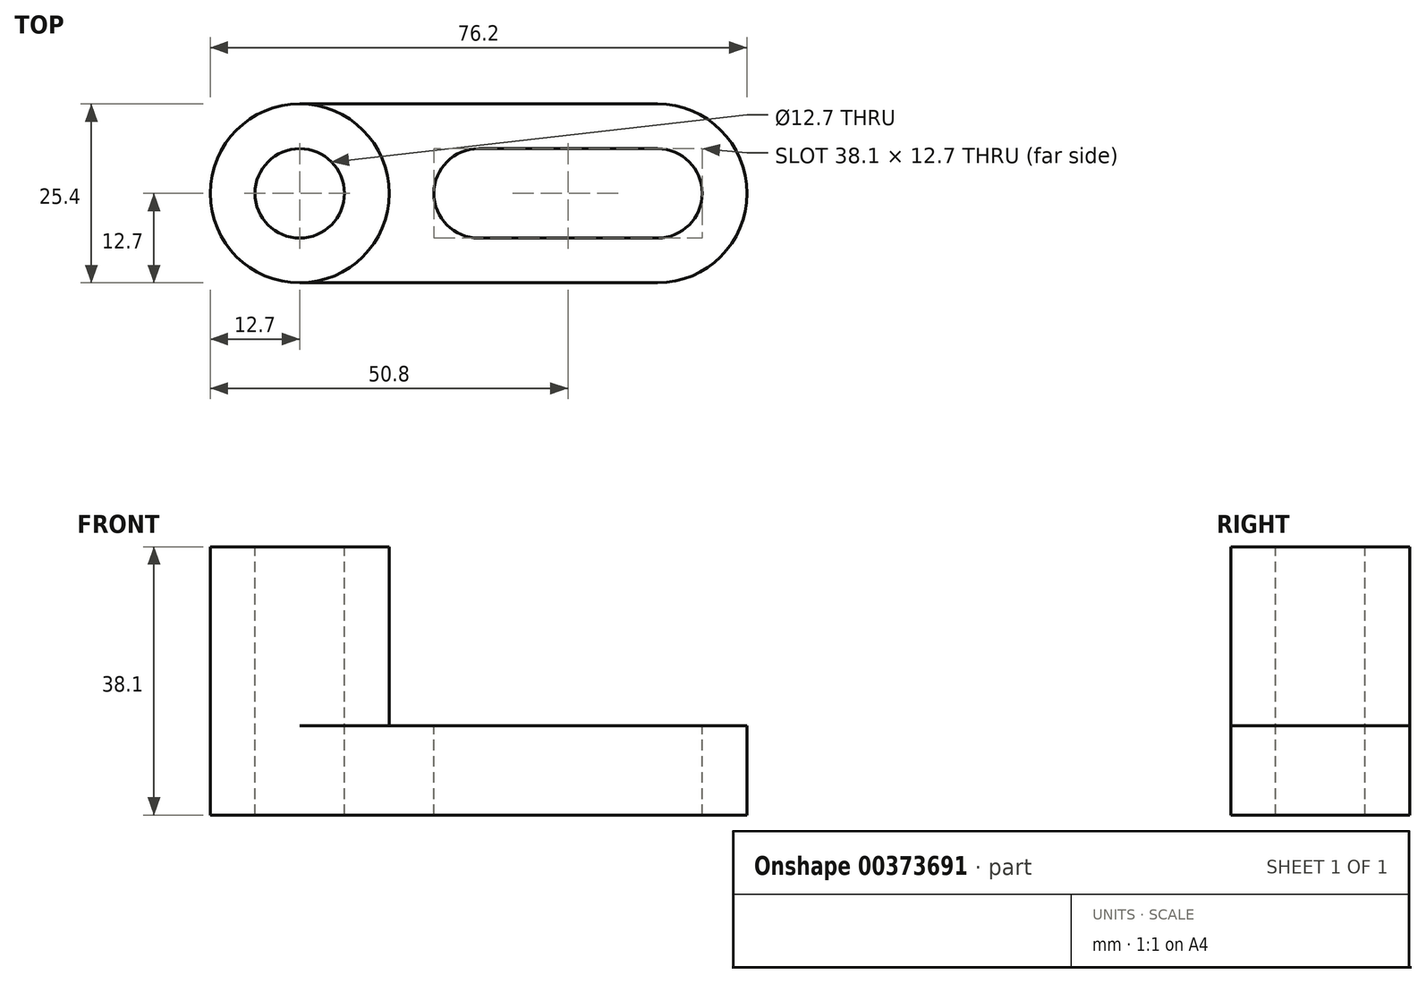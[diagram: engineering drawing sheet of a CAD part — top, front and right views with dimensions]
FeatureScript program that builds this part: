
annotation { "Feature Type Name" : "Feature", "Feature Type Description" : "" }
export const myFeature = defineFeature(function(context is Context, id is Id, definition is map)
    precondition{}
    {
        {
            var Q0;
            Q0=qCreatedBy(makeId("Front.planeOp"),FACE);
            var sketch = newSketch(context, id + "F0", { "sketchPlane" : qUnion([Q0])});
            skLineSegment(sketch, "E0", {"start": v(0, 0) * mm, "end": v(76.2, 0) * mm});
            skLineSegment(sketch, "E1", {"start": v(76.2, 12.7) * mm, "end": v(25.4, 12.7) * mm});
            skLineSegment(sketch, "E2", {"start": v(25.4, 12.7) * mm, "end": v(25.4, 38.1) * mm});
            skLineSegment(sketch, "E3", {"start": v(25.4, 38.1) * mm, "end": v(0, 38.1) * mm});
            skLineSegment(sketch, "E4", {"start": v(0, 38.1) * mm, "end": v(0, 0) * mm});
            skLineSegment(sketch, "E5", {"start": v(76.2, 12.7) * mm, "end": v(76.2, 0) * mm});
            skSolve(sketch);
        }
        {
            var Q0;
            Q0=makeQuery(id+"F0.imprint","IMPRINT",FACE,{"disambiguationData":[TD([[makeQuery(id+"F0.imprint","IMPRINT",EDGE,{"derivedFrom":sQuery(id+"F0.wireOp",EDGE,"E0")}),1.0]])]});
            extrude(context, id + "F1", {"entities" : qUnion([Q0]), "depth" : 25.4 * mm});
        }
        {
            var Q0;
            Q0=makeQuery(id+"F1.opExtrude","SWEPT_FACE",FACE,{"disambiguationData":[OSD([sQuery(id+"F0.wireOp",EDGE,"E3")])]});
            var sketch = newSketch(context, id + "F2", { "sketchPlane" : qUnion([Q0])});
            skCircle(sketch, "E6", {"center": v(12.7, -12.7) * mm, "radius": 12.7 * mm});
            skPoint(sketch, "E6.centerSnap0", {"position": v(25.4, -12.7) * mm});
            skPoint(sketch, "E6.centerSnap1", {"position": v(12.7, 0) * mm});
            skCircle(sketch, "E7", {"center": v(12.7, -12.7) * mm, "radius": 6.35 * mm});
            skSolve(sketch);
        }
        {
            var Q0;
            {var subQ0=sQuery(id+"F2.wireOp",EDGE,"E6");var subQ1=sQuery(id+"F0.wireOp",EDGE,"E3");var subQ2=makeQuery(id+"F1.opExtrude","CAP_EDGE",EDGE,{"disambiguationData":[OSD([subQ1])],"isStart":true});var subQ3=makeQuery(id+"F2.imprint","INTERSECT",VERTEX,{"derivedFrom":[subQ2,subQ0]});Q0=makeQuery(id+"F2.imprint","IMPRINT",FACE,{"disambiguationData":[TD([[makeQuery(id+"F2.imprint","IMPRINT",EDGE,{"disambiguationData":[TD([[subQ3,-1.0]])],"derivedFrom":subQ0}),-1.0]])]});}
            var Q1;
            {var subQ0=sQuery(id+"F2.wireOp",EDGE,"E6");var subQ1=sQuery(id+"F0.wireOp",EDGE,"E3");var subQ4=makeQuery(id+"F1.opExtrude","CAP_EDGE",EDGE,{"disambiguationData":[OSD([subQ1])],"isStart":false});var subQ5=makeQuery(id+"F2.imprint","INTERSECT",VERTEX,{"derivedFrom":[subQ4,subQ0]});Q1=makeQuery(id+"F2.imprint","IMPRINT",FACE,{"disambiguationData":[TD([[makeQuery(id+"F2.imprint","IMPRINT",EDGE,{"disambiguationData":[TD([[subQ5,1.0]])],"derivedFrom":subQ0}),-1.0]])]});}
            var Q2;
            Q2=makeQuery(id+"F2.imprint","IMPRINT",FACE,{"disambiguationData":[TD([[makeQuery(id+"F2.imprint","IMPRINT",EDGE,{"derivedFrom":sQuery(id+"F2.wireOp",EDGE,"E7")}),1.0]])]});
            extrude(context, id + "F3", {"entities" : qUnion([Q0, Q1, Q2]), "operationType" : NewBodyOperationType.REMOVE, "oppositeDirection" : true, "depth" : 50.8 * mm});
        }
        {
            var Q0;
            {var subQ0=sQuery(id+"F2.wireOp",EDGE,"E6");var subQ1=sQuery(id+"F0.wireOp",EDGE,"E3");var subQ2=makeQuery(id+"F1.opExtrude","CAP_EDGE",EDGE,{"disambiguationData":[OSD([subQ1])],"isStart":true});var subQ3=makeQuery(id+"F2.imprint","INTERSECT",VERTEX,{"derivedFrom":[subQ2,subQ0]});Q0=makeQuery(id+"F2.imprint","IMPRINT",FACE,{"disambiguationData":[TD([[makeQuery(id+"F2.imprint","IMPRINT",EDGE,{"disambiguationData":[TD([[subQ3,1.0]])],"derivedFrom":subQ0}),-1.0]])]});}
            var Q1;
            {var subQ0=sQuery(id+"F2.wireOp",EDGE,"E6");var subQ1=sQuery(id+"F0.wireOp",EDGE,"E3");var subQ4=makeQuery(id+"F1.opExtrude","CAP_EDGE",EDGE,{"disambiguationData":[OSD([subQ1])],"isStart":false});var subQ5=makeQuery(id+"F2.imprint","INTERSECT",VERTEX,{"derivedFrom":[subQ4,subQ0]});Q1=makeQuery(id+"F2.imprint","IMPRINT",FACE,{"disambiguationData":[TD([[makeQuery(id+"F2.imprint","IMPRINT",EDGE,{"disambiguationData":[TD([[subQ5,-1.0]])],"derivedFrom":subQ0}),-1.0]])]});}
            extrude(context, id + "F4", {"entities" : qUnion([Q0, Q1]), "operationType" : NewBodyOperationType.REMOVE, "oppositeDirection" : true, "depth" : 25.4 * mm});
        }
        {
            var Q0;
            {var subQ0=sQuery(id+"F0.wireOp",EDGE,"E3");var subQ1=makeQuery(id+"F1.opExtrude","CAP_EDGE",EDGE,{"disambiguationData":[OSD([subQ0])],"isStart":false});var subQ2=sQuery(id+"F0.wireOp",EDGE,"E2");var subQ3=makeQuery(id+"F1.opExtrude","SWEPT_EDGE",EDGE,{"disambiguationData":[OSD([subQ2,subQ0])]});var subQ4=makeQuery(id+"F2.imprint","INTERSECT",VERTEX,{"derivedFrom":[subQ3,subQ1]});var subQ5=sQuery(id+"F2.wireOp",EDGE,"E6");var subQ6=makeQuery(id+"F2.imprint","INTERSECT",VERTEX,{"derivedFrom":[subQ1,subQ5]});var subQ8=makeQuery(id+"F1.opExtrude","CAP_EDGE",EDGE,{"disambiguationData":[OSD([subQ0])],"isStart":true});var subQ9=makeQuery(id+"F2.imprint","INTERSECT",VERTEX,{"derivedFrom":[subQ3,subQ8]});var subQ10=makeQuery(id+"F2.imprint","INTERSECT",VERTEX,{"derivedFrom":[subQ8,subQ5]});Q0=makeQuery(id+"F4.boolean.opBoolean","MERGE",FACE,{"derivedFrom":[makeQuery(id+"F1.opExtrude","SWEPT_FACE",FACE,{"disambiguationData":[OSD([sQuery(id+"F0.wireOp",EDGE,"E1")])]}),makeQuery(id+"F4.opExtrude","CAP_FACE",FACE,{"disambiguationData":[OSD([subQ2,subQ0,subQ5]),TDD([makeQuery(id+"F2.imprint","IMPRINT",EDGE,{"disambiguationData":[TD([[subQ10,1.0]])],"derivedFrom":subQ5}),makeQuery(id+"F2.imprint","IMPRINT",EDGE,{"disambiguationData":[TD([[subQ9,1.0]])],"derivedFrom":subQ3}),makeQuery(id+"F2.imprint","IMPRINT",EDGE,{"disambiguationData":[TD([[subQ10,1.0]])],"derivedFrom":subQ8})])],"isStart":false}),makeQuery(id+"F4.opExtrude","CAP_FACE",FACE,{"disambiguationData":[OSD([subQ2,subQ0,subQ5]),TDD([makeQuery(id+"F2.imprint","IMPRINT",EDGE,{"disambiguationData":[TD([[subQ6,-1.0]])],"derivedFrom":subQ5}),makeQuery(id+"F2.imprint","IMPRINT",EDGE,{"disambiguationData":[TD([[subQ4,-1.0]])],"derivedFrom":subQ3}),makeQuery(id+"F2.imprint","IMPRINT",EDGE,{"disambiguationData":[TD([[subQ6,1.0]])],"derivedFrom":subQ1})])],"isStart":false})]});}
            var sketch = newSketch(context, id + "F5", { "sketchPlane" : qUnion([Q0])});
            skCircle(sketch, "E8", {"center": v(38.1, -12.7) * mm, "radius": 6.35 * mm});
            skPoint(sketch, "E8.centerSnap0", {"position": v(25.4, -12.7) * mm});
            skCircle(sketch, "E9", {"center": v(63.5, -12.7) * mm, "radius": 6.35 * mm});
            skLineSegment(sketch, "E10", {"start": v(63.5, -19.05) * mm, "end": v(38.1, -19.05) * mm});
            skLineSegment(sketch, "E11", {"start": v(38.1, -19.05) * mm, "end": v(38.1, -6.35) * mm});
            skLineSegment(sketch, "E12", {"start": v(38.1, -6.35) * mm, "end": v(63.5, -6.35) * mm});
            skLineSegment(sketch, "E13", {"start": v(63.5, -6.35) * mm, "end": v(63.5, -19.05) * mm});
            skArc(sketch, "E14", {"start": v(63.5, -25.4) * mm, "mid": v(76.2, -12.7) * mm, "end": v(63.5, 0) * mm});
            skSolve(sketch);
        }
        {
            var Q0;
            {var subQ0=sQuery(id+"F5.wireOp",EDGE,"E13");Q0=makeQuery(id+"F5.imprint","IMPRINT",FACE,{"disambiguationData":[TD([[makeQuery(id+"F5.imprint","IMPRINT",EDGE,{"derivedFrom":subQ0}),1.0]])]});}
            var Q1;
            {var subQ0=sQuery(id+"F5.wireOp",EDGE,"E11");Q1=makeQuery(id+"F5.imprint","IMPRINT",FACE,{"disambiguationData":[TD([[makeQuery(id+"F5.imprint","IMPRINT",EDGE,{"derivedFrom":subQ0}),1.0]])]});}
            var Q2;
            {var subQ0=sQuery(id+"F5.wireOp",EDGE,"E11");Q2=makeQuery(id+"F5.imprint","IMPRINT",FACE,{"disambiguationData":[TD([[makeQuery(id+"F5.imprint","IMPRINT",EDGE,{"derivedFrom":subQ0}),-1.0]])]});}
            var Q3;
            {var subQ1=sQuery(id+"F5.wireOp",EDGE,"E10");Q3=makeQuery(id+"F5.imprint","IMPRINT",FACE,{"disambiguationData":[TD([[makeQuery(id+"F5.imprint","IMPRINT",EDGE,{"derivedFrom":subQ1}),-1.0]])]});}
            var Q4;
            {var subQ0=sQuery(id+"F5.wireOp",EDGE,"E14");var subQ3=sQuery(id+"F0.wireOp",EDGE,"E1");var subQ6=makeQuery(id+"F1.opExtrude","SWEPT_EDGE",EDGE,{"disambiguationData":[OSD([subQ3,sQuery(id+"F0.wireOp",EDGE,"E5")])]});var subQ7=makeQuery(id+"F5.imprint","INTERSECT",VERTEX,{"derivedFrom":[subQ6,subQ0]});Q4=makeQuery(id+"F5.imprint","IMPRINT",FACE,{"disambiguationData":[TD([[makeQuery(id+"F5.imprint","IMPRINT",EDGE,{"disambiguationData":[TD([[subQ7,1.0]])],"derivedFrom":subQ0}),-1.0]])]});}
            var Q5;
            {var subQ0=sQuery(id+"F5.wireOp",EDGE,"E14");var subQ3=sQuery(id+"F0.wireOp",EDGE,"E1");var subQ6=makeQuery(id+"F1.opExtrude","SWEPT_EDGE",EDGE,{"disambiguationData":[OSD([subQ3,sQuery(id+"F0.wireOp",EDGE,"E5")])]});var subQ7=makeQuery(id+"F5.imprint","INTERSECT",VERTEX,{"derivedFrom":[subQ6,subQ0]});Q5=makeQuery(id+"F5.imprint","IMPRINT",FACE,{"disambiguationData":[TD([[makeQuery(id+"F5.imprint","IMPRINT",EDGE,{"disambiguationData":[TD([[subQ7,-1.0]])],"derivedFrom":subQ0}),-1.0]])]});}
            var Q6;
            {var subQ0=sQuery(id+"F5.wireOp",EDGE,"E13");Q6=makeQuery(id+"F5.imprint","IMPRINT",FACE,{"disambiguationData":[TD([[makeQuery(id+"F5.imprint","IMPRINT",EDGE,{"derivedFrom":subQ0}),-1.0]])]});}
            extrude(context, id + "F6", {"entities" : qUnion([Q0, Q1, Q2, Q3, Q4, Q5, Q6]), "operationType" : NewBodyOperationType.REMOVE, "oppositeDirection" : true, "depth" : 25.4 * mm});
        }
    });
